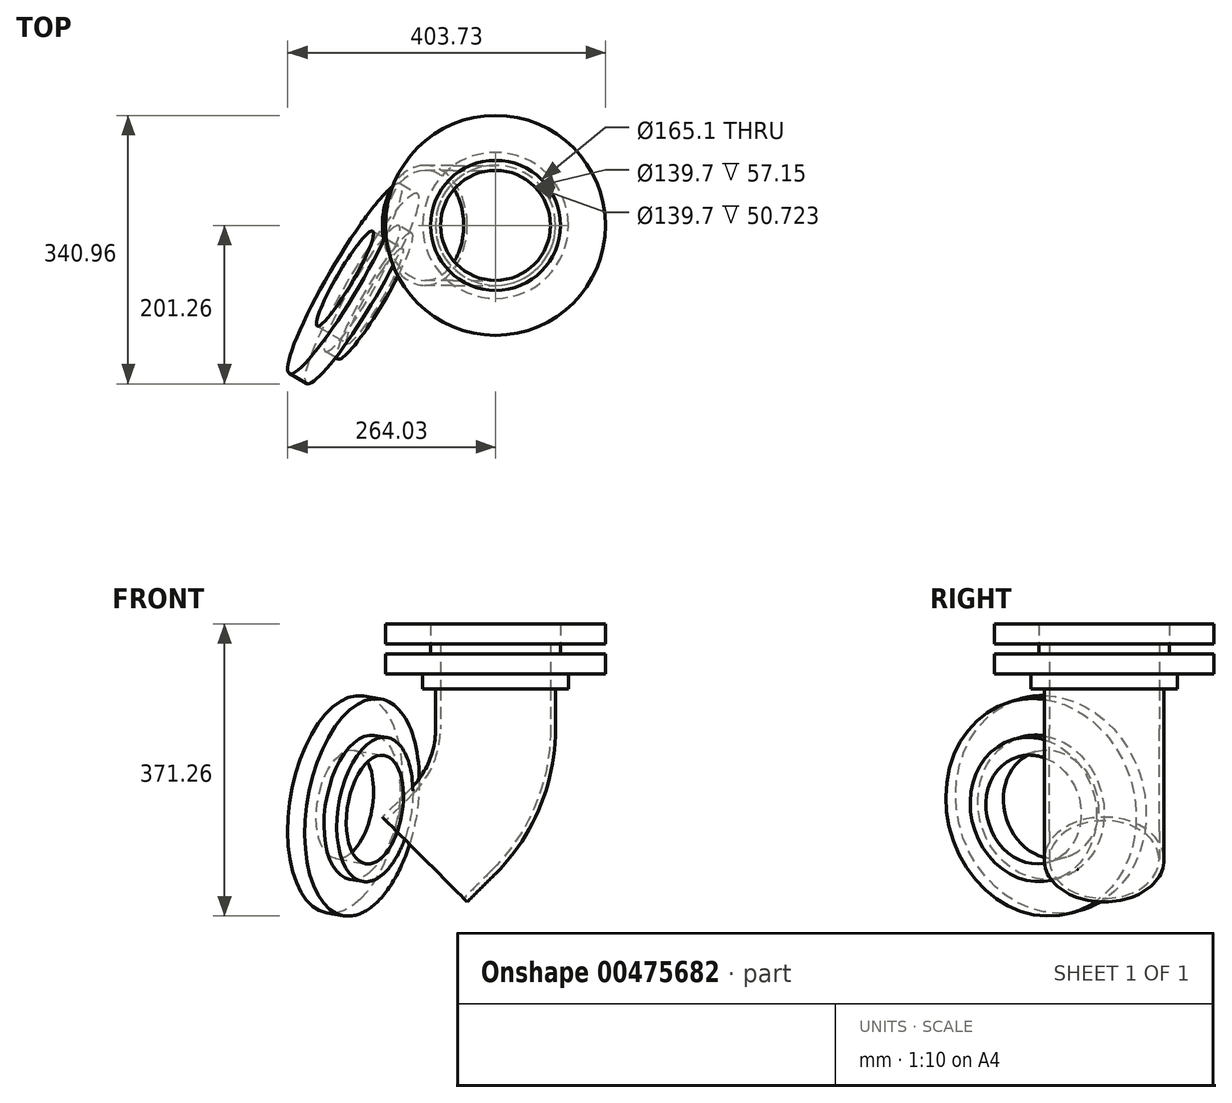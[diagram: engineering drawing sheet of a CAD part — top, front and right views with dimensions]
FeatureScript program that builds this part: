
annotation { "Feature Type Name" : "Feature", "Feature Type Description" : "" }
export const myFeature = defineFeature(function(context is Context, id is Id, definition is map)
    precondition{}
    {
        {
            var Q0;
            Q0=qCreatedBy(makeId("Top.planeOp"),FACE);
            var sketch = newSketch(context, id + "F0", { "sketchPlane" : qUnion([Q0])});
            skCircle(sketch, "E0", {"center": v(0, 0) * mm, "radius": 69.85 * mm});
            skCircle(sketch, "E1", {"center": v(0, 0) * mm, "radius": 76.2 * mm});
            skSolve(sketch);
        }
        {
            var Q0;
            Q0=makeQuery(id+"F0.imprint","IMPRINT",FACE,{"disambiguationData":[TD([[makeQuery(id+"F0.imprint","IMPRINT",EDGE,{"derivedFrom":sQuery(id+"F0.wireOp",EDGE,"E0")}),-1.0]])]});
            extrude(context, id + "F1", {"entities" : qUnion([Q0]), "depth" : 19.05 * mm});
        }
        {
            var Q0;
            Q0=makeQuery(id+"F1.opExtrude","CAP_FACE",FACE,{"disambiguationData":[OSD([sQuery(id+"F0.wireOp",EDGE,"E0"),sQuery(id+"F0.wireOp",EDGE,"E1")])],"isStart":false});
            var sketch = newSketch(context, id + "F2", { "sketchPlane" : qUnion([Q0])});
            skCircle(sketch, "E2", {"center": v(0, 0) * mm, "radius": 139.7 * mm});
            skCircle(sketch, "E3", {"center": v(0, 0) * mm, "radius": 92.7 * mm});
            skSolve(sketch);
        }
        {
            var Q0;
            Q0=makeQuery(id+"F2.imprint","IMPRINT",FACE,{"disambiguationData":[TD([[makeQuery(id+"F2.imprint","IMPRINT",EDGE,{"derivedFrom":sQuery(id+"F2.wireOp",EDGE,"E2")}),1.0]])]});
            var Q1;
            Q1=makeQuery(id+"F2.imprint","IMPRINT",FACE,{"disambiguationData":[TD([[makeQuery(id+"F2.imprint","IMPRINT",EDGE,{"derivedFrom":makeQuery(id+"F1.opExtrude","CAP_EDGE",EDGE,{"disambiguationData":[OSD([sQuery(id+"F0.wireOp",EDGE,"E0")])],"isStart":false})}),-1.0]])]});
            var Q2;
            Q2=makeQuery(id+"F2.imprint","IMPRINT",FACE,{"disambiguationData":[TD([[makeQuery(id+"F2.imprint","IMPRINT",EDGE,{"derivedFrom":sQuery(id+"F2.wireOp",EDGE,"E3")}),1.0]])]});
            extrude(context, id + "F3", {"entities" : qUnion([Q0, Q1, Q2]), "operationType" : NewBodyOperationType.ADD, "depth" : 25.4 * mm});
        }
        {
            var Q0;
            Q0=makeQuery(id+"F2.imprint","IMPRINT",FACE,{"disambiguationData":[TD([[makeQuery(id+"F2.imprint","IMPRINT",EDGE,{"derivedFrom":sQuery(id+"F2.wireOp",EDGE,"E3")}),1.0]])]});
            extrude(context, id + "F4", {"entities" : qUnion([Q0]), "operationType" : NewBodyOperationType.ADD, "oppositeDirection" : true, "depth" : 19.05 * mm});
        }
        {
            var Q0;
            Q0=qCreatedBy(makeId("Front.planeOp"),FACE);
            var sketch = newSketch(context, id + "F5", { "sketchPlane" : qUnion([Q0])});
            skLineSegment(sketch, "E4", {"start": v(0, 0) * mm, "end": v(0, -50.72) * mm});
            skLineSegment(sketch, "E5", {"start": v(-53.94, -180.94) * mm, "end": v(-89.8, -216.8) * mm});
            skPoint(sketch, "E6.visualSharp", {"position": v(0, -127) * mm});
            skArc(sketch, "E6.filletArc", {"start": v(-53.94, -180.94) * mm, "mid": v(-14.02, -121.2) * mm, "end": v(0, -50.72) * mm});
            skSolve(sketch);
        }
        {
            var Q0;
            Q0=makeQuery(id+"F0.imprint","IMPRINT",FACE,{"disambiguationData":[TD([[makeQuery(id+"F0.imprint","IMPRINT",EDGE,{"derivedFrom":sQuery(id+"F0.wireOp",EDGE,"E0")}),-1.0]])]});
            var Q1;
            Q1=sQuery(id+"F5.wireOp",EDGE,"E6.filletArc");
            var Q2;
            Q2=sQuery(id+"F5.wireOp",EDGE,"E5");
            var Q3;
            Q3=sQuery(id+"F5.wireOp",EDGE,"E4");
            sweep(context, id + "F6", {"profiles" : qUnion([Q0]), "path" : qUnion([Q1, Q2, Q3])});
        }
        {
            var Q0;
            Q0=makeQuery(id+"F6.opSweep","CAP_FACE",FACE,{"disambiguationData":[OSD([sQuery(id+"F0.wireOp",EDGE,"E0"),sQuery(id+"F0.wireOp",EDGE,"E1"),sQuery(id+"F5.wireOp",VERTEX,"E5.end")])],"isStart":false});
            var sketch = newSketch(context, id + "F7", { "sketchPlane" : qUnion([Q0])});
            skPoint(sketch, "E7", {"position": v(89.8, 0) * mm});
            skLineSegment(sketch, "E8", {"start": v(89.8, 0) * mm, "end": v(89.8, 343.85) * mm, "construction": true});
            skSolve(sketch);
        }
        {
            var Q0;
            Q0=makeQuery(id+"F1.opExtrude","SWEPT_BODY",BODY,{"disambiguationData":[OSD([sQuery(id+"F0.wireOp",EDGE,"E0"),sQuery(id+"F0.wireOp",EDGE,"E1")])]});
            var Q1;
            Q1=qCreatedBy(makeId("Origin.pointOp"),VERTEX);
            var Q2;
            Q2=sQuery(id+"F7.wireOp",VERTEX,"E7");
            transform(context, id + "F8", {"entities" : qUnion([Q0]), "transformType" : TransformType.TRANSLATION_ENTITY, "oppositeDirectionEntity" : false, "transformLine" : qUnion([Q1, Q2]), "makeCopy" : true});
        }
        {
            var Q0;
            Q0=makeQuery(id+"F8.opPattern","COPY",BODY,{"derivedFrom":makeQuery(id+"F1.opExtrude","SWEPT_BODY",BODY,{"disambiguationData":[OSD([sQuery(id+"F0.wireOp",EDGE,"E0"),sQuery(id+"F0.wireOp",EDGE,"E1")])]}),"instanceName":"1"});
            var Q1;
            Q1=sQuery(id+"F7.wireOp",VERTEX,"E7");
            var Q2;
            Q2=sQuery(id+"F7.wireOp",EDGE,"E8");
            transform(context, id + "F9", {"entities" : qUnion([Q0]), "transformType" : TransformType.ROTATION, "transformAxis" : qUnion([Q2]), "angle" : 135 * degree, "makeCopy" : false});
        }
        {
            var Q0;
            Q0=makeQuery(id+"F3.opExtrude","CAP_FACE",FACE,{"disambiguationData":[OSD([sQuery(id+"F0.wireOp",EDGE,"E0"),sQuery(id+"F2.wireOp",EDGE,"E2")])],"isStart":false});
            var sketch = newSketch(context, id + "F10", { "sketchPlane" : qUnion([Q0])});
            skCircle(sketch, "E9", {"center": v(0, 0) * mm, "radius": 82.55 * mm});
            skSolve(sketch);
        }
        {
            var Q0;
            Q0=makeQuery(id+"F10.imprint","IMPRINT",FACE,{"disambiguationData":[TD([[makeQuery(id+"F10.imprint","IMPRINT",EDGE,{"derivedFrom":sQuery(id+"F10.wireOp",EDGE,"E9")}),1.0]])]});
            extrude(context, id + "F11", {"entities" : qUnion([Q0]), "operationType" : NewBodyOperationType.ADD, "depth" : 12.7 * mm});
        }
        {
            var Q0;
            Q0=makeQuery(id+"F11.opExtrude","CAP_FACE",FACE,{"disambiguationData":[OSD([sQuery(id+"F0.wireOp",EDGE,"E0"),sQuery(id+"F10.wireOp",EDGE,"E9")])],"isStart":false});
            var sketch = newSketch(context, id + "F12", { "sketchPlane" : qUnion([Q0])});
            skCircle(sketch, "E10", {"center": v(0, 0) * mm, "radius": 139.7 * mm});
            skSolve(sketch);
        }
        {
            var Q0;
            Q0=makeQuery(id+"F12.imprint","IMPRINT",FACE,{"disambiguationData":[TD([[makeQuery(id+"F12.imprint","IMPRINT",EDGE,{"derivedFrom":sQuery(id+"F12.wireOp",EDGE,"E10")}),1.0]])]});
            extrude(context, id + "F13", {"entities" : qUnion([Q0]), "operationType" : NewBodyOperationType.ADD, "depth" : 25.4 * mm});
        }
    });
